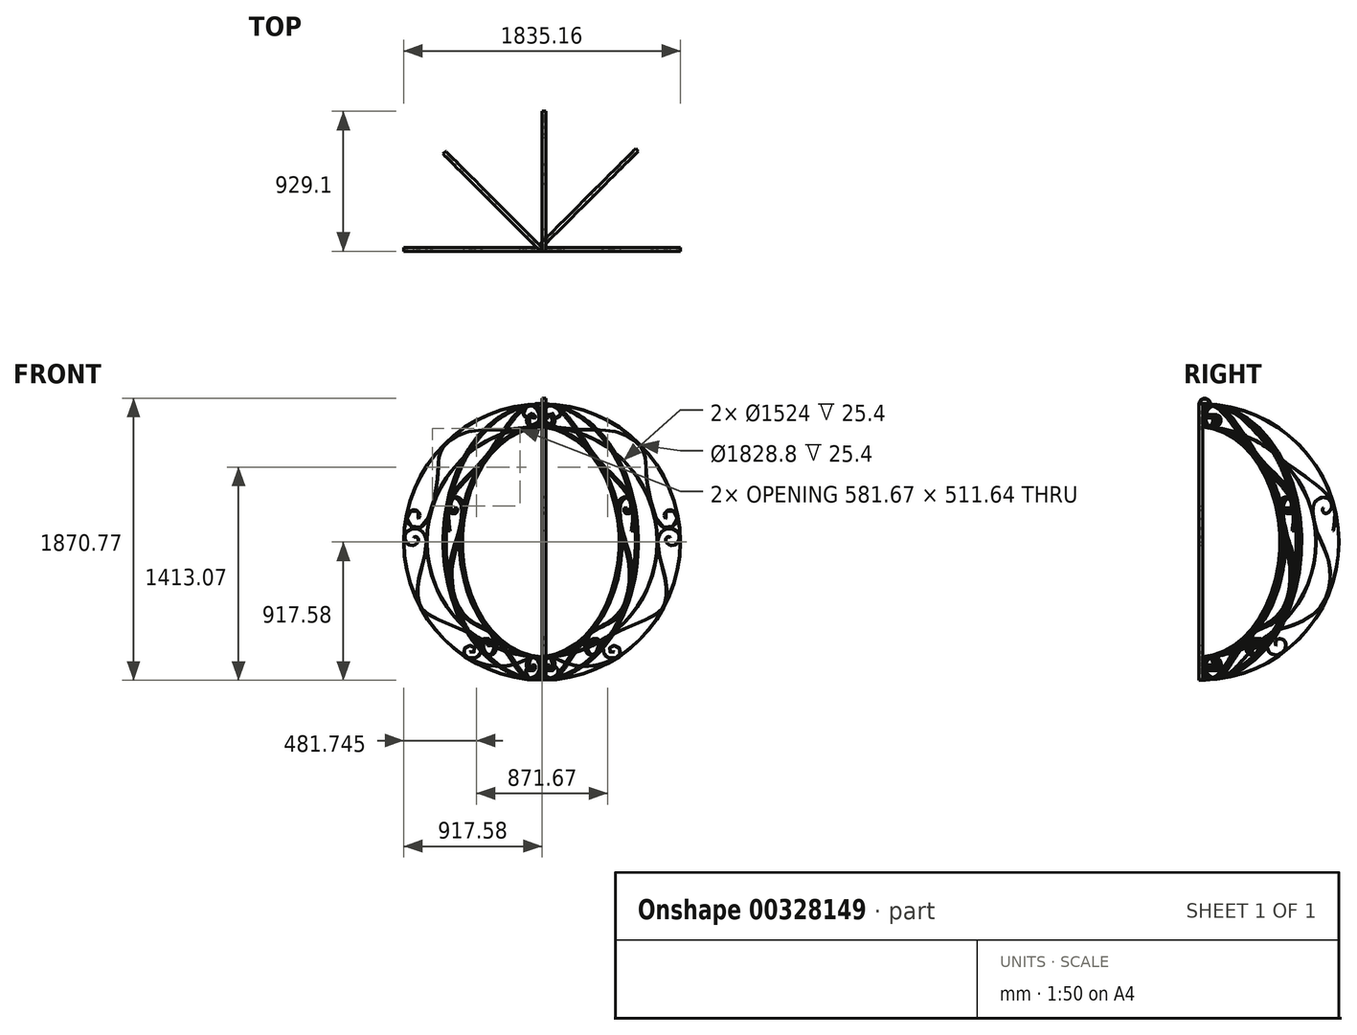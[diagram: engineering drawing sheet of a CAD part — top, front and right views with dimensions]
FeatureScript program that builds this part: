
annotation { "Feature Type Name" : "Feature", "Feature Type Description" : "" }
export const myFeature = defineFeature(function(context is Context, id is Id, definition is map)
    precondition{}
    {
        {
            var Q0;
            Q0=qCreatedBy(makeId("Front.planeOp"),FACE);
            var sketch = newSketch(context, id + "F0", { "sketchPlane" : qUnion([Q0])});
            skCircle(sketch, "E0", {"center": v(0, 0) * mm, "radius": 914.4 * mm});
            skCircle(sketch, "E1.0", {"center": v(0, 0) * mm, "radius": 917.58 * mm});
            skSolve(sketch);
        }
        {
            var Q0;
            Q0 = qSketchRegion(id + "F0", true);
            extrude(context, id + "F1", {"entities" : qUnion([Q0]), "depth" : 25.4 * mm});
        }
        {
            var Q0;
            Q0=qCreatedBy(makeId("Front.planeOp"),FACE);
            var sketch = newSketch(context, id + "F2", { "sketchPlane" : qUnion([Q0])});
            skCircle(sketch, "E2", {"center": v(0, 0) * mm, "radius": 762 * mm});
            skCircle(sketch, "E3.0", {"center": v(0, 0) * mm, "radius": 765.18 * mm});
            skSolve(sketch);
        }
        {
            var Q0;
            Q0 = qSketchRegion(id + "F2", true);
            extrude(context, id + "F3", {"entities" : qUnion([Q0]), "depth" : 25.4 * mm});
        }
        {
            var Q0;
            Q0=qCreatedBy(makeId("Right.planeOp"),FACE);
            var sketch = newSketch(context, id + "F4", { "sketchPlane" : qUnion([Q0])});
            skArc(sketch, "E4", {"start": v(0, -917.18) * mm, "mid": v(903.58, 0.32) * mm, "end": v(0, 917.8) * mm});
            skArc(sketch, "E5.0", {"start": v(-0.05, -914) * mm, "mid": v(900.4, 0.32) * mm, "end": v(-0.05, 914.63) * mm});
            skLineSegment(sketch, "E6", {"start": v(0, 917.8) * mm, "end": v(-0.05, 914.63) * mm});
            skLineSegment(sketch, "E7", {"start": v(0, -917.18) * mm, "end": v(-0.05, -914) * mm});
            skSolve(sketch);
        }
        {
            var Q0;
            Q0 = qSketchRegion(id + "F4", true);
            extrude(context, id + "F5", {"entities" : qUnion([Q0]), "depth" : 25.4 * mm});
        }
        {
            var Q0;
            Q0=qCreatedBy(makeId("Right.planeOp"),FACE);
            var sketch = newSketch(context, id + "F6", { "sketchPlane" : qUnion([Q0])});
            skArc(sketch, "E8.0", {"start": v(-2.38, -761.62) * mm, "mid": v(748, 0.32) * mm, "end": v(-2.38, 762.25) * mm});
            skArc(sketch, "E9.0", {"start": v(-2.33, -764.8) * mm, "mid": v(751.18, 0.32) * mm, "end": v(-2.33, 765.43) * mm});
            skLineSegment(sketch, "E10", {"start": v(-2.33, 765.43) * mm, "end": v(-2.38, 762.25) * mm});
            skLineSegment(sketch, "E11", {"start": v(-2.38, -761.62) * mm, "end": v(-2.33, -764.8) * mm});
            skSolve(sketch);
        }
        {
            var Q0;
            Q0 = qSketchRegion(id + "F6", true);
            extrude(context, id + "F7", {"entities" : qUnion([Q0]), "depth" : 25.4 * mm});
        }
        {
            var Q0;
            Q0=qCreatedBy(makeId("Front.planeOp"),FACE);
            var sketch = newSketch(context, id + "F8", { "sketchPlane" : qUnion([Q0])});
            skFitSpline(sketch, "E12", {"points": [v(-766.38, 0) * mm, v(-837.55, 89.66) * mm, v(-910.52, 47.32) * mm, v(-875.84, -22.95) * mm, v(-820.43, 0) * mm, v(-827.64, 32) * mm, v(-851.96, 32.9) * mm], "startDerivative": vector(22.8, 710.17) * mm, "endDerivative": vector(-220.68, -142.8) * mm});
            skFitSpline(sketch, "E13.0", {"points": [v(-769.55, 0.1) * mm, v(-769.32, 7.3) * mm, v(-770.23, 20.87) * mm, v(-775.14, 38.64) * mm, v(-783.04, 53.79) * mm, v(-793.39, 66.24) * mm, v(-805.67, 75.92) * mm, v(-817.08, 81.59) * mm, v(-826.65, 84.63) * mm, v(-833.97, 86.15) * mm, v(-841.37, 86.89) * mm, v(-848.8, 86.87) * mm, v(-856.18, 86.12) * mm, v(-865.82, 84.18) * mm, v(-877.28, 80.11) * mm, v(-887.37, 74.08) * mm, v(-894.27, 68.25) * mm, v(-898.78, 63.41) * mm, v(-902.56, 58.16) * mm, v(-905.03, 53.46) * mm, v(-906.57, 49.53) * mm, v(-907.5, 46.5) * mm, v(-908.2, 43.37) * mm, v(-908.82, 39.08) * mm, v(-909.04, 33.54) * mm, v(-908.47, 26.73) * mm, v(-907.1, 19.9) * mm, v(-904.28, 10.9) * mm, v(-900.1, 2.4) * mm, v(-894.8, -5.1) * mm, v(-890.37, -10.09) * mm, v(-885.52, -14.33) * mm, v(-881.2, -17.13) * mm, v(-877.64, -18.9) * mm, v(-874.9, -19.96) * mm, v(-872.12, -20.77) * mm, v(-868.3, -21.52) * mm, v(-863.42, -21.86) * mm, v(-857.45, -21.4) * mm, v(-851.53, -20.12) * mm, v(-845.77, -18.13) * mm, v(-840.33, -15.51) * mm, v(-835.32, -12.36) * mm, v(-830.9, -8.79) * mm, v(-827.8, -5.55) * mm, v(-825.74, -2.86) * mm, v(-824.41, -0.82) * mm, v(-823.32, 1.23) * mm, v(-822.18, 3.98) * mm, v(-821.3, 7.47) * mm, v(-821.02, 11.64) * mm, v(-821.46, 15.71) * mm, v(-822.54, 19.6) * mm, v(-824.18, 23.18) * mm, v(-826.3, 26.33) * mm, v(-828.77, 28.95) * mm, v(-831.5, 30.94) * mm, v(-834.46, 32.33) * mm, v(-837.57, 33.13) * mm, v(-840.78, 33.34) * mm, v(-845.1, 32.82) * mm, v(-848.26, 31.52) * mm, v(-850.24, 30.24) * mm]});
            skLineSegment(sketch, "E14", {"start": v(-851.96, 32.9) * mm, "end": v(-850.24, 30.24) * mm});
            skLineSegment(sketch, "E15", {"start": v(-769.54, 0.6) * mm, "end": v(-766.38, 0) * mm});
            skFitSpline(sketch, "E16", {"points": [v(-766.38, 0) * mm, v(-810.04, -219.1) * mm, v(-823.98, -348.98) * mm, v(-806.41, -421.67) * mm, v(-750.28, -479.94) * mm, v(-511.26, -589.61) * mm, v(-410.71, -659.86) * mm, v(-408.3, -740.12) * mm, v(-452.14, -773.78) * mm, v(-507.86, -758.17) * mm, v(-518.27, -709.63) * mm, v(-480.54, -685.55) * mm, v(-448.1, -700.97) * mm, v(-449.4, -729.8) * mm, v(-479.45, -728.28) * mm], "startDerivative": vector(-67.53, -2503.48) * mm, "endDerivative": vector(-624.87, 867.88) * mm});
            skFitSpline(sketch, "E17.0", {"points": [v(-769.55, 0.09) * mm, v(-770.25, -25.85) * mm, v(-773.72, -60.69) * mm, v(-781.3, -101.2) * mm, v(-788, -129.16) * mm, v(-795.25, -155.26) * mm, v(-801.36, -175.92) * mm, v(-806.06, -192.06) * mm, v(-809.43, -204.05) * mm, v(-812.58, -215.99) * mm, v(-815.46, -227.93) * mm, v(-818.03, -239.86) * mm, v(-821.07, -255.7) * mm, v(-824.13, -275.3) * mm, v(-826.58, -298.2) * mm, v(-827.59, -316.6) * mm, v(-827.77, -330.75) * mm, v(-827.59, -341.06) * mm, v(-827.08, -351.04) * mm, v(-826.26, -360.65) * mm, v(-825.1, -369.9) * mm, v(-823.14, -381.8) * mm, v(-820.52, -393.03) * mm, v(-817.25, -403.66) * mm, v(-814.47, -411.34) * mm, v(-811.89, -417.5) * mm, v(-809.65, -422.3) * mm, v(-807.31, -427) * mm, v(-804.16, -432.75) * mm, v(-799.9, -439.46) * mm, v(-795.08, -446) * mm, v(-789.62, -452.44) * mm, v(-783.43, -458.78) * mm, v(-776.42, -465.09) * mm, v(-768.5, -471.4) * mm, v(-761.08, -476.7) * mm, v(-754.6, -480.98) * mm, v(-747.73, -485.3) * mm, v(-738.46, -490.8) * mm, v(-726.32, -497.48) * mm, v(-713.3, -504.26) * mm, v(-699.5, -511.11) * mm, v(-680.2, -520.31) * mm, v(-654.74, -531.88) * mm, v(-622.93, -545.72) * mm, v(-590.8, -559.33) * mm, v(-564.55, -570.34) * mm, v(-544.34, -578.87) * mm, v(-529.7, -585.1) * mm, v(-518, -590.13) * mm, v(-509.04, -594.05) * mm, v(-500.33, -597.9) * mm, v(-489.94, -602.62) * mm, v(-478.28, -608.18) * mm, v(-467.45, -613.72) * mm, v(-454.12, -621.16) * mm, v(-442.48, -628.82) * mm, v(-432.58, -636.96) * mm, v(-426.02, -643.37) * mm, v(-420.33, -650.15) * mm, v(-416.3, -656.18) * mm, v(-413.5, -661.28) * mm, v(-411.63, -665.25) * mm, v(-409.95, -669.35) * mm, v(-408, -674.99) * mm, v(-406.07, -682.28) * mm, v(-404.09, -694.27) * mm, v(-403.75, -706.43) * mm, v(-405, -718.15) * mm, v(-406.72, -726.57) * mm, v(-408.78, -733.13) * mm, v(-410.8, -738.03) * mm, v(-413.05, -742.68) * mm, v(-416.3, -748.02) * mm, v(-420.85, -753.68) * mm, v(-425.99, -758.6) * mm, v(-431.66, -762.74) * mm, v(-437.83, -766.13) * mm, v(-444.43, -768.74) * mm, v(-451.42, -770.56) * mm, v(-458.75, -771.58) * mm, v(-466.29, -771.77) * mm, v(-473.85, -771.13) * mm, v(-481.26, -769.66) * mm, v(-488.36, -767.37) * mm, v(-494.98, -764.25) * mm, v(-499.97, -760.98) * mm, v(-503.58, -757.97) * mm, v(-506.07, -755.52) * mm, v(-508.35, -752.85) * mm, v(-511.1, -749.05) * mm, v(-513.96, -743.9) * mm, v(-516.44, -737.29) * mm, v(-517.9, -730.48) * mm, v(-518.28, -723.71) * mm, v(-517.68, -718.29) * mm, v(-516.63, -714.19) * mm, v(-515.75, -711.75) * mm, v(-514.9, -709.87) * mm, v(-513.95, -708.05) * mm, v(-512.59, -705.85) * mm, v(-510.69, -703.36) * mm, v(-507.84, -700.26) * mm, v(-503.74, -696.8) * mm, v(-498.14, -693.4) * mm, v(-492.1, -690.84) * mm, v(-486.87, -689.47) * mm, v(-482.68, -688.86) * mm, v(-479.57, -688.65) * mm, v(-476.5, -688.69) * mm, v(-472.48, -689.06) * mm, v(-467.65, -690.1) * mm, v(-462.32, -692.2) * mm, v(-457.6, -695.06) * mm, v(-454.3, -698) * mm, v(-452.1, -700.64) * mm, v(-450.68, -702.76) * mm, v(-449.5, -705.01) * mm, v(-448.25, -708.17) * mm, v(-447.32, -712.32) * mm, v(-447.26, -717.32) * mm, v(-448.11, -721.26) * mm, v(-449.33, -724.15) * mm, v(-450.52, -726.16) * mm, v(-451.97, -728) * mm, v(-453.73, -729.66) * mm, v(-455.75, -731.1) * mm, v(-458.69, -732.63) * mm, v(-461.9, -733.5) * mm, v(-465.15, -733.6) * mm, v(-467.58, -733.24) * mm, v(-469.98, -732.42) * mm, v(-472.35, -731.09) * mm, v(-474.66, -729.16) * mm, v(-476.15, -727.42) * mm, v(-476.87, -726.42) * mm]});
            skLineSegment(sketch, "E18", {"start": v(-476.87, -726.42) * mm, "end": v(-479.45, -728.28) * mm});
            skLineSegment(sketch, "E19", {"start": v(-769.54, 0.6) * mm, "end": v(-769.55, 0.09) * mm});
            skSolve(sketch);
        }
        {
            var Q0;
            Q0 = qSketchRegion(id + "F8", true);
            extrude(context, id + "F9", {"entities" : qUnion([Q0]), "depth" : 25.4 * mm});
        }
        {
            var Q0;
            Q0=qCreatedBy(makeId("Front.planeOp"),FACE);
            var sketch = newSketch(context, id + "F10", { "sketchPlane" : qUnion([Q0])});
            skFitSpline(sketch, "E20", {"points": [v(-820.36, 153.24) * mm, v(-841.55, 212.18) * mm, v(-892.93, 185.39) * mm, v(-881.98, 116.68) * mm, v(-813.57, 92.5) * mm, v(-752.31, 165.46) * mm, v(-689.96, 435.02) * mm, v(-666.43, 608.75) * mm, v(-499.45, 727.2) * mm, v(-204.24, 745.98) * mm, v(0, 812.46) * mm, v(-26.01, 898.7) * mm, v(-99.89, 903.2) * mm, v(-127.82, 855) * mm, v(-91.33, 819.42) * mm, v(-62.97, 856.62) * mm], "startDerivative": vector(1522.53, 1759.37) * mm, "endDerivative": vector(-990.2, 1432.62) * mm});
            skFitSpline(sketch, "E21.0", {"points": [v(-822.76, 155.31) * mm, v(-820.87, 157.5) * mm, v(-817.7, 161.76) * mm, v(-814.56, 167.83) * mm, v(-812.87, 173.51) * mm, v(-812.4, 178.82) * mm, v(-813.03, 183.8) * mm, v(-814.61, 188.46) * mm, v(-817.06, 192.8) * mm, v(-820.26, 196.8) * mm, v(-824.1, 200.36) * mm, v(-828.45, 203.46) * mm, v(-833.16, 206.02) * mm, v(-837.25, 207.67) * mm, v(-840.55, 208.68) * mm, v(-843.84, 209.47) * mm, v(-847.9, 210.06) * mm, v(-852.7, 210.16) * mm, v(-858.95, 209.53) * mm, v(-866.42, 207.4) * mm, v(-874.6, 202.92) * mm, v(-880.57, 197.8) * mm, v(-884.67, 193.02) * mm, v(-887.39, 189.13) * mm, v(-889.7, 184.96) * mm, v(-891.6, 180.54) * mm, v(-893.07, 175.9) * mm, v(-894.46, 169.47) * mm, v(-895.16, 161.07) * mm, v(-894.32, 150.73) * mm, v(-891.86, 140.49) * mm, v(-888.49, 132.31) * mm, v(-885.03, 126.15) * mm, v(-882.06, 121.76) * mm, v(-878.72, 117.64) * mm, v(-875.01, 113.81) * mm, v(-870.98, 110.28) * mm, v(-865.21, 105.98) * mm, v(-857.38, 101.43) * mm, v(-847.34, 97.38) * mm, v(-837, 94.86) * mm, v(-828.42, 94.11) * mm, v(-821.77, 94.36) * mm, v(-816.92, 94.98) * mm, v(-812.27, 96.04) * mm, v(-806.31, 98.03) * mm, v(-799.26, 101.63) * mm, v(-791.3, 107.7) * mm, v(-781.24, 118.13) * mm, v(-771.9, 132) * mm, v(-763.03, 149.04) * mm, v(-756.54, 163.35) * mm, v(-750.13, 179.1) * mm, v(-741.72, 201.83) * mm, v(-731.61, 233.05) * mm, v(-720.45, 273.67) * mm, v(-712.24, 309.06) * mm, v(-706.5, 337.65) * mm, v(-702.64, 359.06) * mm, v(-699.28, 380.28) * mm, v(-696.93, 397.66) * mm, v(-695.34, 411.31) * mm, v(-694.3, 421.4) * mm, v(-693.41, 431.31) * mm, v(-692.7, 441.03) * mm, v(-692.11, 450.56) * mm, v(-691.5, 463.03) * mm, v(-690.97, 478.18) * mm, v(-690.48, 495.7) * mm, v(-689.73, 518.26) * mm, v(-688.4, 539.71) * mm, v(-685.6, 560.23) * mm, v(-682.54, 575.2) * mm, v(-679, 587.35) * mm, v(-675.44, 596.89) * mm, v(-672.4, 603.95) * mm, v(-668.95, 610.94) * mm, v(-665.07, 617.84) * mm, v(-660.77, 624.63) * mm, v(-654.52, 633.54) * mm, v(-645.76, 644.4) * mm, v(-633.83, 656.88) * mm, v(-620.62, 668.78) * mm, v(-601.44, 683.77) * mm, v(-574.8, 700.72) * mm, v(-545.38, 714.84) * mm, v(-520.62, 724.17) * mm, v(-501.54, 730.12) * mm, v(-482.09, 734.95) * mm, v(-455.7, 740.02) * mm, v(-421.92, 744.13) * mm, v(-380.25, 746.46) * mm, v(-337.58, 747.14) * mm, v(-294.04, 747.12) * mm, v(-257.16, 747.31) * mm, v(-227.36, 748.06) * mm, v(-204.88, 749.04) * mm, v(-182.28, 750.55) * mm, v(-152.34, 753.34) * mm, v(-115.93, 758.4) * mm, v(-82.65, 765.86) * mm, v(-58.99, 773.43) * mm, v(-43, 779.95) * mm, v(-29.04, 787.33) * mm, v(-19.33, 794.2) * mm, v(-12.84, 800.12) * mm, v(-8.63, 804.78) * mm, v(-5.7, 808.84) * mm, v(-3.7, 812.2) * mm, v(-1.93, 815.62) * mm, v(-0.17, 820.07) * mm, v(1.78, 827.49) * mm, v(2.64, 837.21) * mm, v(1.35, 849.22) * mm, v(-2.05, 861.13) * mm, v(-7.3, 872.5) * mm, v(-12.98, 881.15) * mm, v(-18.19, 887.37) * mm, v(-22.38, 891.63) * mm, v(-26.82, 895.43) * mm, v(-31.47, 898.72) * mm, v(-36.32, 901.52) * mm, v(-43.01, 904.62) * mm, v(-51.71, 907.32) * mm, v(-62.41, 908.78) * mm, v(-73.08, 908.53) * mm, v(-83.42, 906.69) * mm, v(-91.51, 903.9) * mm, v(-97.52, 900.97) * mm, v(-103.18, 897.59) * mm, v(-109.55, 892.58) * mm, v(-115.87, 885.56) * mm, v(-120.7, 877.79) * mm, v(-123.85, 869.51) * mm, v(-124.97, 862.4) * mm, v(-124.89, 857.4) * mm, v(-124.58, 854.56) * mm, v(-124.1, 851.7) * mm, v(-123.2, 848.16) * mm, v(-121.1, 842.64) * mm, v(-117.35, 836.17) * mm, v(-112.3, 830.75) * mm, v(-107.62, 827.3) * mm, v(-103.82, 825.22) * mm, v(-99.76, 823.68) * mm, v(-96.17, 822.9) * mm, v(-93.18, 822.62) * mm, v(-90.12, 822.56) * mm, v(-86.11, 822.93) * mm, v(-81.24, 824.07) * mm, v(-76.5, 825.85) * mm, v(-72.12, 828.2) * mm, v(-68.3, 831.03) * mm, v(-65.2, 834.26) * mm, v(-63.01, 837.79) * mm, v(-61.8, 841.52) * mm, v(-61.64, 845.51) * mm, v(-62.7, 849.9) * mm, v(-64.41, 853.13) * mm, v(-65.58, 854.81) * mm]});
            skLineSegment(sketch, "E22", {"start": v(-822.76, 155.31) * mm, "end": v(-820.36, 153.24) * mm});
            skLineSegment(sketch, "E23", {"start": v(-62.97, 856.62) * mm, "end": v(-65.58, 854.81) * mm});
            skSolve(sketch);
        }
        {
            var Q0;
            Q0 = qSketchRegion(id + "F10", true);
            extrude(context, id + "F11", {"entities" : qUnion([Q0]), "operationType" : NewBodyOperationType.ADD, "depth" : 25.4 * mm});
        }
        {
            var Q0;
            Q0=makeQuery(id+"F3.opExtrude","SWEPT_BODY",BODY,{"disambiguationData":[OSD([sQuery(id+"F2.wireOp",EDGE,"E2"),sQuery(id+"F2.wireOp",EDGE,"E3.0")])]});
            var Q1;
            Q1=makeQuery(id+"F9.opExtrude","SWEPT_BODY",BODY,{"disambiguationData":[OSD([sQuery(id+"F8.wireOp",EDGE,"E12"),sQuery(id+"F8.wireOp",EDGE,"E13.0"),sQuery(id+"F8.wireOp",EDGE,"E14"),sQuery(id+"F8.wireOp",EDGE,"E16"),sQuery(id+"F8.wireOp",EDGE,"E17.0"),sQuery(id+"F8.wireOp",EDGE,"E18"),sQuery(id+"F8.wireOp",EDGE,"E19")])]});
            var Q2;
            Q2=qCreatedBy(makeId("Right.planeOp"),FACE);
            mirror(context, id + "F12", {"entities" : qUnion([Q0, Q1]), "mirrorPlane" : qUnion([Q2])});
        }
        {
            var Q0;
            Q0=qCreatedBy(makeId("Front.planeOp"),FACE);
            var sketch = newSketch(context, id + "F13", { "sketchPlane" : qUnion([Q0])});
            skFitSpline(sketch, "E24", {"points": [v(-464.75, -784.96) * mm, v(-336.85, -822.2) * mm, v(-177.25, -811.88) * mm, v(-50.25, -767.12) * mm, v(6.22, -822.74) * mm, v(-19.78, -898.37) * mm, v(-84.79, -899.63) * mm, v(-106.14, -857) * mm, v(-87.31, -826.93) * mm, v(-50.93, -839.36) * mm], "startDerivative": vector(1405.33, -534.22) * mm, "endDerivative": vector(261.46, -709.68) * mm});
            skFitSpline(sketch, "E25.0", {"points": [v(-463.62, -781.99) * mm, v(-448.99, -787.55) * mm, v(-430.27, -794.58) * mm, v(-409.86, -801.8) * mm, v(-396.34, -806.28) * mm, v(-384.13, -809.93) * mm, v(-372.74, -812.88) * mm, v(-361.68, -815.27) * mm, v(-352.3, -816.9) * mm, v(-344.47, -818.04) * mm, v(-338.36, -818.83) * mm, v(-331.95, -819.58) * mm, v(-323.03, -820.5) * mm, v(-311.2, -821.5) * mm, v(-296.15, -822.34) * mm, v(-280.38, -822.72) * mm, v(-264.08, -822.53) * mm, v(-247.43, -821.7) * mm, v(-230.6, -820.11) * mm, v(-213.78, -817.68) * mm, v(-199.9, -814.87) * mm, v(-188.97, -812.1) * mm, v(-180.89, -809.75) * mm, v(-172.93, -807.12) * mm, v(-165.1, -804.22) * mm, v(-157.37, -801.12) * mm, v(-147.22, -796.75) * mm, v(-134.82, -791.03) * mm, v(-120.4, -784.1) * mm, v(-106.4, -777.55) * mm, v(-92.85, -771.76) * mm, v(-79.67, -767.15) * mm, v(-68.98, -764.65) * mm, v(-60.58, -763.7) * mm, v(-55.4, -763.58) * mm, v(-51.29, -763.8) * mm, v(-47.2, -764.26) * mm, v(-42.2, -765.25) * mm, v(-36.37, -767.07) * mm, v(-28.88, -770.28) * mm, v(-20.12, -775.65) * mm, v(-10.75, -783.92) * mm, v(-2.76, -793.73) * mm, v(2.6, -802.93) * mm, v(6, -810.76) * mm, v(8.06, -816.83) * mm, v(9.63, -823.07) * mm, v(10.66, -829.41) * mm, v(11.18, -835.81) * mm, v(11.2, -844.37) * mm, v(10.02, -854.98) * mm, v(6.77, -867.24) * mm, v(1.8, -878.68) * mm, v(-3.73, -887.23) * mm, v(-8.93, -893.3) * mm, v(-13.21, -897.41) * mm, v(-17.1, -900.44) * mm, v(-20.38, -902.58) * mm, v(-23.76, -904.54) * mm, v(-28.15, -906.65) * mm, v(-35.44, -909.3) * mm, v(-44.93, -911.31) * mm, v(-56.47, -911.75) * mm, v(-65.85, -910.54) * mm, v(-73.01, -908.66) * mm, v(-78.15, -906.8) * mm, v(-82.2, -904.87) * mm, v(-85.26, -903.11) * mm, v(-88.2, -901.2) * mm, v(-91.62, -898.56) * mm, v(-96.51, -893.86) * mm, v(-101.57, -887.23) * mm, v(-105.94, -878.48) * mm, v(-108.63, -869.3) * mm, v(-109.48, -861.62) * mm, v(-109.31, -855.62) * mm, v(-108.57, -849.78) * mm, v(-106.6, -842.85) * mm, v(-102.55, -835.4) * mm, v(-97.81, -830.11) * mm, v(-93.25, -826.6) * mm, v(-89.46, -824.35) * mm, v(-85.3, -822.51) * mm, v(-80.87, -821.16) * mm, v(-76.24, -820.35) * mm, v(-71.5, -820.2) * mm, v(-66.76, -820.79) * mm, v(-62.12, -822.24) * mm, v(-57.74, -824.64) * mm, v(-53.8, -828.08) * mm, v(-50.45, -832.55) * mm, v(-48.7, -836.24) * mm, v(-47.95, -838.26) * mm]});
            skLineSegment(sketch, "E26", {"start": v(-463.62, -781.99) * mm, "end": v(-464.75, -784.96) * mm});
            skLineSegment(sketch, "E27", {"start": v(-47.95, -838.26) * mm, "end": v(-50.93, -839.36) * mm});
            skSolve(sketch);
        }
        {
            var Q0;
            Q0 = qSketchRegion(id + "F13", true);
            extrude(context, id + "F14", {"entities" : qUnion([Q0]), "depth" : 25.4 * mm});
        }
        {
            var Q0;
            Q0=makeQuery(id+"F14.opExtrude","SWEPT_BODY",BODY,{"disambiguationData":[OSD([sQuery(id+"F13.wireOp",EDGE,"E24"),sQuery(id+"F13.wireOp",EDGE,"E25.0"),sQuery(id+"F13.wireOp",EDGE,"E26"),sQuery(id+"F13.wireOp",EDGE,"E27")])]});
            var Q1;
            Q1=qCreatedBy(makeId("Right.planeOp"),FACE);
            mirror(context, id + "F15", {"operationType" : NewBodyOperationType.ADD, "entities" : qUnion([Q0]), "mirrorPlane" : qUnion([Q1])});
        }
        {
            var Q0;
            Q0=qCreatedBy(makeId("Right.planeOp"),FACE);
            var sketch = newSketch(context, id + "F16", { "sketchPlane" : qUnion([Q0])});
            skFitSpline(sketch, "E28", {"points": [v(58.89, 821.78) * mm, v(105.76, 839.02) * mm, v(112.38, 781.02) * mm, v(35.54, 767.65) * mm, v(0, 825.81) * mm, v(31.08, 887.16) * mm, v(132.75, 900.64) * mm, v(346.4, 734.22) * mm, v(538.07, 539.86) * mm, v(836.34, 299.56) * mm, v(877.14, 163) * mm, v(865, 72.14) * mm], "startDerivative": vector(89.14, 1381.73) * mm, "endDerivative": vector(-221.8, -1107.85) * mm});
            skFitSpline(sketch, "E29.0", {"points": [v(62.06, 821.58) * mm, v(62.16, 823.22) * mm, v(62.6, 826.25) * mm, v(63.87, 830.12) * mm, v(65.63, 833.36) * mm, v(67.83, 836.05) * mm, v(70.43, 838.25) * mm, v(74.39, 840.54) * mm, v(80.13, 842.26) * mm, v(87.74, 842.48) * mm, v(94.12, 841.2) * mm, v(98.9, 839.36) * mm, v(101.7, 837.9) * mm, v(103.77, 836.56) * mm, v(105.73, 835.1) * mm, v(108.88, 832.27) * mm, v(112.58, 827.43) * mm, v(115.73, 820.64) * mm, v(117.53, 813.2) * mm, v(117.94, 805.42) * mm, v(116.95, 797.69) * mm, v(114.96, 791.56) * mm, v(112.67, 787.02) * mm, v(110.61, 783.83) * mm, v(108.2, 780.9) * mm, v(105.44, 778.18) * mm, v(102.35, 775.7) * mm, v(97.83, 772.73) * mm, v(91.5, 769.62) * mm, v(83.1, 766.92) * mm, v(71.17, 764.73) * mm, v(58.72, 764.7) * mm, v(46.89, 766.85) * mm, v(39.98, 769.1) * mm, v(34.9, 771.42) * mm, v(30.09, 774.1) * mm, v(24.6, 778.05) * mm, v(18.87, 783.66) * mm, v(12.36, 792.12) * mm, v(7.6, 801.78) * mm, v(4.65, 812.07) * mm, v(3.58, 818.64) * mm, v(3.2, 823.91) * mm, v(3.12, 829.16) * mm, v(3.61, 835.67) * mm, v(5.1, 843.34) * mm, v(8.25, 853.3) * mm, v(14.26, 865.14) * mm, v(24.51, 877.85) * mm, v(37.53, 888.6) * mm, v(53.02, 896.9) * mm, v(70.75, 902.37) * mm, v(87.18, 904.19) * mm, v(101.2, 903.78) * mm, v(112.12, 902.5) * mm, v(123.4, 900.16) * mm, v(135.04, 896.72) * mm, v(147, 892.15) * mm, v(163.33, 884.64) * mm, v(184.35, 872.8) * mm, v(210.18, 855.28) * mm, v(236.26, 835.09) * mm, v(262.28, 812.84) * mm, v(283.62, 793.12) * mm, v(300.34, 776.94) * mm, v(312.66, 764.7) * mm, v(324.71, 752.4) * mm, v(334.51, 742.2) * mm, v(342.18, 734.08) * mm, v(349.72, 726.03) * mm, v(358.94, 716.06) * mm, v(369.72, 704.24) * mm, v(383.8, 688.66) * mm, v(401, 669.46) * mm, v(421.54, 646.76) * mm, v(442.47, 624.25) * mm, v(464.29, 601.83) * mm, v(483.63, 583.1) * mm, v(500.06, 568.05) * mm, v(512.9, 556.7) * mm, v(524.12, 547.19) * mm, v(533.42, 539.53) * mm, v(542.95, 531.84) * mm, v(555.28, 522.18) * mm, v(570.64, 510.51) * mm, v(586.48, 498.77) * mm, v(608.1, 483.03) * mm, v(635.83, 463.2) * mm, v(669.48, 439.25) * mm, v(702.72, 415.18) * mm, v(734.8, 391.08) * mm, v(764.94, 367) * mm, v(787.8, 347.03) * mm, v(804.34, 331.14) * mm, v(815.79, 319.29) * mm, v(824.43, 309.47) * mm, v(830.77, 301.65) * mm, v(836.7, 293.87) * mm, v(843.36, 284.2) * mm, v(850.22, 272.67) * mm, v(856.04, 261.24) * mm, v(862.5, 246.15) * mm, v(868.35, 227.58) * mm, v(872.43, 205.84) * mm, v(873.88, 188.25) * mm, v(874.19, 174.54) * mm, v(874.05, 164.45) * mm, v(873.65, 154.56) * mm, v(872.77, 141.66) * mm, v(871.13, 126) * mm, v(868.47, 107.83) * mm, v(865.32, 90.11) * mm, v(863.04, 78.53) * mm, v(861.88, 72.76) * mm]});
            skLineSegment(sketch, "E30", {"start": v(58.89, 821.78) * mm, "end": v(62.06, 821.58) * mm});
            skLineSegment(sketch, "E31", {"start": v(861.88, 72.76) * mm, "end": v(865, 72.14) * mm});
            skSolve(sketch);
        }
        {
            var Q0;
            Q0 = qSketchRegion(id + "F16", true);
            extrude(context, id + "F17", {"entities" : qUnion([Q0]), "depth" : 25.4 * mm});
        }
        {
            var Q0;
            Q0=qCreatedBy(makeId("Right.planeOp"),FACE);
            var sketch = newSketch(context, id + "F18", { "sketchPlane" : qUnion([Q0])});
            skFitSpline(sketch, "E32", {"points": [v(833, 192.73) * mm, v(858.99, 238.6) * mm, v(822.76, 294.38) * mm, v(739, 262.86) * mm, v(766.82, 40.25) * mm, v(837.49, -148.84) * mm, v(787.26, -420.34) * mm, v(575.48, -557.66) * mm, v(454.42, -604.84) * mm, v(420.89, -673.4) * mm, v(454.8, -743.96) * mm, v(533.65, -730.04) * mm, v(544.13, -657.03) * mm, v(490.71, -646.47) * mm, v(485.85, -687.83) * mm], "startDerivative": vector(737.01, 571.07) * mm, "endDerivative": vector(709.47, -766.23) * mm});
            skFitSpline(sketch, "E33", {"points": [v(833, 192.73) * mm, v(801.88, 192.73) * mm, v(796.21, 227.08) * mm], "startDerivative": vector(-54.77, -28.8) * mm, "endDerivative": vector(41.92, 61.2) * mm});
            skFitSpline(sketch, "E34.0", {"points": [v(831.05, 195.24) * mm, v(834.7, 198.07) * mm, v(840.33, 203.44) * mm, v(846.9, 212.3) * mm, v(851.04, 219.65) * mm, v(853.6, 226.24) * mm, v(854.99, 231.73) * mm, v(855.66, 235.94) * mm, v(855.93, 240.23) * mm, v(855.79, 244.62) * mm, v(855.23, 249.06) * mm, v(853.96, 255) * mm, v(851.4, 262.35) * mm, v(846.88, 270.72) * mm, v(841, 278.33) * mm, v(835.08, 283.77) * mm, v(829.77, 287.42) * mm, v(825.52, 289.79) * mm, v(821.02, 291.73) * mm, v(816.25, 293.24) * mm, v(811.25, 294.3) * mm, v(804.33, 295.14) * mm, v(795.34, 295.08) * mm, v(784.36, 293.23) * mm, v(773.57, 289.61) * mm, v(763.35, 284.25) * mm, v(755.6, 278.36) * mm, v(750.02, 272.8) * mm, v(746.2, 268.2) * mm, v(742.76, 263.2) * mm, v(739.78, 257.76) * mm, v(737.23, 251.88) * mm, v(734.38, 243.49) * mm, v(731.84, 232) * mm, v(730.32, 216.84) * mm, v(730.2, 195.09) * mm, v(733.27, 165.54) * mm, v(739.8, 134.28) * mm, v(746.55, 109.07) * mm, v(752.23, 90.27) * mm, v(758.4, 71.79) * mm, v(763.82, 56.82) * mm, v(768.27, 45.2) * mm, v(771.64, 36.7) * mm, v(775.03, 28.4) * mm, v(779.57, 17.6) * mm, v(785.27, 4.5) * mm, v(792.07, -10.66) * mm, v(798.76, -25.44) * mm, v(807.46, -44.8) * mm, v(815.69, -63.95) * mm, v(823.17, -83.45) * mm, v(828.33, -98.38) * mm, v(832.97, -113.76) * mm, v(837.03, -129.73) * mm, v(840.43, -146.42) * mm, v(843.1, -163.97) * mm, v(845.01, -182.27) * mm, v(846.13, -201.18) * mm, v(846.4, -220.58) * mm, v(845.64, -246.92) * mm, v(842.45, -280.41) * mm, v(834.77, -320.49) * mm, v(824.94, -352.91) * mm, v(814.88, -377.75) * mm, v(806.2, -395.7) * mm, v(797.97, -409.98) * mm, v(790.8, -420.93) * mm, v(785.1, -428.88) * mm, v(779.12, -436.58) * mm, v(770.79, -446.5) * mm, v(759.73, -458.27) * mm, v(745.57, -471.43) * mm, v(725.66, -487.75) * mm, v(699.2, -505.92) * mm, v(665.92, -524.5) * mm, v(637.77, -537.55) * mm, v(615.5, -546.68) * mm, v(599.06, -552.9) * mm, v(585.67, -557.61) * mm, v(575.21, -561.1) * mm, v(564.94, -564.43) * mm, v(552.48, -568.3) * mm, v(538.16, -572.62) * mm, v(524.52, -576.76) * mm, v(511.59, -580.84) * mm, v(499.42, -585.01) * mm, v(488.04, -589.39) * mm, v(477.51, -594.1) * mm, v(467.85, -599.27) * mm, v(460.56, -604.06) * mm, v(455.18, -608.24) * mm, v(450.11, -612.69) * mm, v(444.35, -618.7) * mm, v(438.37, -626.59) * mm, v(433.37, -635.08) * mm, v(429.39, -644.11) * mm, v(426.45, -653.62) * mm, v(424.6, -663.54) * mm, v(423.86, -673.8) * mm, v(424.3, -684.36) * mm, v(425.88, -694.91) * mm, v(428.62, -705.2) * mm, v(432.5, -714.9) * mm, v(437.5, -723.79) * mm, v(442.58, -730.27) * mm, v(447.17, -734.78) * mm, v(450.88, -737.8) * mm, v(454.2, -740) * mm, v(456.97, -741.54) * mm, v(459.85, -742.94) * mm, v(463.62, -744.44) * mm, v(469.96, -746.3) * mm, v(478.36, -747.58) * mm, v(488.87, -747.49) * mm, v(499.44, -745.79) * mm, v(509.72, -742.52) * mm, v(517.75, -738.52) * mm, v(523.68, -734.6) * mm, v(527.84, -731.3) * mm, v(531.67, -727.64) * mm, v(535.15, -723.62) * mm, v(538.28, -719.3) * mm, v(541.95, -713.17) * mm, v(545.59, -704.98) * mm, v(548.32, -694.73) * mm, v(549.34, -684.5) * mm, v(548.7, -676.37) * mm, v(547.3, -670.32) * mm, v(545.8, -666.06) * mm, v(544.16, -662.77) * mm, v(542.62, -660.33) * mm, v(541.36, -658.6) * mm, v(539.97, -656.95) * mm, v(537.97, -654.87) * mm, v(535.2, -652.5) * mm, v(531.5, -650.02) * mm, v(526.19, -647.26) * mm, v(519.01, -644.87) * mm, v(510.2, -643.79) * mm, v(503.24, -644.45) * mm, v(498.23, -645.92) * mm, v(495.4, -647.22) * mm, v(493.33, -648.48) * mm, v(491.41, -649.9) * mm, v(489.24, -651.97) * mm, v(487.03, -654.88) * mm, v(484.64, -659.22) * mm, v(482.75, -665.31) * mm, v(482.43, -672.91) * mm, v(483.85, -678.83) * mm, v(485.99, -682.98) * mm, v(487.4, -684.82) * mm, v(488.18, -685.67) * mm]});
            skFitSpline(sketch, "E35.0", {"points": [v(831.51, 195.54) * mm, v(829.45, 194.46) * mm, v(825.87, 193.04) * mm, v(820.7, 191.92) * mm, v(816.76, 191.54) * mm, v(812.92, 191.69) * mm, v(809.9, 192.27) * mm, v(807.65, 193.04) * mm, v(806.06, 193.77) * mm, v(804.57, 194.66) * mm, v(803.19, 195.7) * mm, v(801.88, 196.96) * mm, v(800.25, 198.87) * mm, v(798.48, 201.67) * mm, v(796.86, 205.5) * mm, v(795.85, 209.64) * mm, v(795.49, 213.88) * mm, v(795.83, 218.03) * mm, v(796.9, 221.91) * mm, v(798.1, 224.22) * mm, v(798.83, 225.28) * mm]});
            skLineSegment(sketch, "E36", {"start": v(796.21, 227.08) * mm, "end": v(798.83, 225.28) * mm});
            skLineSegment(sketch, "E37", {"start": v(485.85, -687.83) * mm, "end": v(488.18, -685.67) * mm});
            skSolve(sketch);
        }
        {
            var Q0;
            Q0 = qSketchRegion(id + "F18", true);
            extrude(context, id + "F19", {"entities" : qUnion([Q0]), "depth" : 25.4 * mm});
        }
        {
            var Q0;
            Q0=qCreatedBy(makeId("Right.planeOp"),FACE);
            var sketch = newSketch(context, id + "F20", { "sketchPlane" : qUnion([Q0])});
            skFitSpline(sketch, "E38", {"points": [v(422.6, -631.86) * mm, v(290.66, -756.8) * mm, v(134.08, -897.5) * mm, v(24.4, -881.6) * mm, v(0, -815.04) * mm, v(52.25, -763.08) * mm, v(113.65, -784.78) * mm, v(110.63, -846.8) * mm, v(68.27, -848.32) * mm, v(68.27, -814.28) * mm], "startDerivative": vector(-622.17, -631.45) * mm, "endDerivative": vector(390.78, 455.9) * mm});
            skFitSpline(sketch, "E39.0", {"points": [v(420.34, -629.63) * mm, v(413.9, -636.16) * mm, v(399.72, -649.77) * mm, v(375.36, -671.9) * mm, v(353.21, -691.88) * mm, v(334.82, -708.86) * mm, v(320.8, -722.1) * mm, v(309, -733.59) * mm, v(299.57, -743.04) * mm, v(292.5, -750.28) * mm, v(285.44, -757.65) * mm, v(276.1, -767.65) * mm, v(264.48, -780.38) * mm, v(250.62, -795.76) * mm, v(236.81, -811) * mm, v(223, -825.85) * mm, v(209.16, -840.06) * mm, v(195.26, -853.38) * mm, v(181.26, -865.55) * mm, v(167.14, -876.32) * mm, v(155.25, -883.93) * mm, v(145.65, -889.08) * mm, v(138.4, -892.44) * mm, v(131.1, -895.28) * mm, v(123.75, -897.57) * mm, v(116.35, -899.35) * mm, v(106.47, -901.05) * mm, v(94.18, -901.95) * mm, v(79.75, -901.2) * mm, v(65.89, -898.75) * mm, v(52.83, -894.72) * mm, v(40.83, -889.25) * mm, v(31.9, -883.6) * mm, v(25.54, -878.51) * mm, v(19.71, -873.06) * mm, v(13.45, -865.61) * mm, v(7.65, -855.92) * mm, v(3.65, -845.7) * mm, v(1.53, -835.17) * mm, v(1.37, -826.33) * mm, v(2.25, -819.32) * mm, v(3.43, -814.12) * mm, v(5.13, -808.98) * mm, v(8.05, -802.26) * mm, v(12.84, -794.2) * mm, v(20.16, -785.38) * mm, v(28.78, -777.72) * mm, v(36.8, -772.54) * mm, v(43.58, -769.27) * mm, v(48.8, -767.29) * mm, v(54.14, -765.8) * mm, v(59.56, -764.83) * mm, v(65.03, -764.38) * mm, v(72.31, -764.44) * mm, v(81.26, -765.75) * mm, v(91.33, -769.23) * mm, v(98.83, -773.65) * mm, v(104.1, -778.05) * mm, v(107.65, -781.78) * mm, v(110.22, -785.23) * mm, v(112.04, -788.2) * mm, v(113.7, -791.32) * mm, v(115.46, -795.44) * mm, v(117.63, -802.43) * mm, v(119.07, -811.62) * mm, v(118.73, -822.6) * mm, v(116.76, -831.01) * mm, v(114.2, -836.91) * mm, v(112.21, -840.18) * mm, v(110.4, -842.5) * mm, v(108.93, -844.08) * mm, v(107.35, -845.5) * mm, v(105.08, -847.22) * mm, v(101.97, -849) * mm, v(97.9, -850.58) * mm, v(93.6, -851.58) * mm, v(89.23, -852) * mm, v(84.89, -851.88) * mm, v(80.72, -851.2) * mm, v(76.86, -850.01) * mm, v(74, -848.63) * mm, v(71.98, -847.3) * mm, v(70.62, -846.21) * mm, v(69.41, -845.02) * mm, v(67.98, -843.29) * mm, v(66.53, -840.88) * mm, v(65.34, -837.65) * mm, v(64.7, -834.17) * mm, v(64.65, -829.32) * mm, v(66.08, -823.1) * mm, v(68.87, -818.46) * mm, v(70.68, -816.35) * mm]});
            skLineSegment(sketch, "E40", {"start": v(419.84, -630.14) * mm, "end": v(422.6, -631.86) * mm});
            skLineSegment(sketch, "E41", {"start": v(70.68, -816.35) * mm, "end": v(68.27, -814.28) * mm});
            skSolve(sketch);
        }
        {
            var Q0;
            Q0 = qSketchRegion(id + "F20", true);
            extrude(context, id + "F21", {"entities" : qUnion([Q0]), "depth" : 25.4 * mm});
        }
        {
            var Q0;
            Q0=qCreatedBy(makeId("Right.planeOp"),FACE);
            var sketch = newSketch(context, id + "F22", { "sketchPlane" : qUnion([Q0])});
            skArc(sketch, "E42", {"start": v(50.36, 914.83) * mm, "mid": v(13.76, 953.17) * mm, "end": v(-25.52, 917.59) * mm});
            skArc(sketch, "E43.0", {"start": v(44.02, 914.9) * mm, "mid": v(13.53, 946.82) * mm, "end": v(-19.18, 917.2) * mm});
            skLineSegment(sketch, "E44", {"start": v(-25.52, 917.59) * mm, "end": v(-19.18, 917.2) * mm});
            skLineSegment(sketch, "E45", {"start": v(44.02, 914.9) * mm, "end": v(50.36, 914.83) * mm});
            skSolve(sketch);
        }
        {
            var Q0;
            Q0 = qSketchRegion(id + "F22", true);
            extrude(context, id + "F23", {"entities" : qUnion([Q0]), "depth" : 25.4 * mm});
        }
        {
            var Q0;
            Q0=makeQuery(id+"F23.opExtrude","CAP_EDGE",EDGE,{"disambiguationData":[OSD([sQuery(id+"F22.wireOp",EDGE,"E43.0")])],"isStart":false});
            fillet(context, id + "F24", {"entities" : qUnion([Q0]), "radius" : 5.08 * mm, "tangentPropagation" : true, "allowEdgeOverflow" : false});
        }
        {
            var Q0;
            Q0=qCreatedBy(makeId("Top.planeOp"),FACE);
            var sketch = newSketch(context, id + "F25", { "sketchPlane" : qUnion([Q0])});
            skLineSegment(sketch, "E46", {"start": v(0, 0) * mm, "end": v(-7.4, -3.06) * mm, "construction": true});
            skLineSegment(sketch, "E47", {"start": v(0, 0) * mm, "end": v(-8.66, 20.92) * mm, "construction": true});
            skSolve(sketch);
        }
        {
            var Q0;
            Q0=sQuery(id+"F25.wireOp",EDGE,"E47");
            cPlane(context, id + "F26", {"entities" : qUnion([Q0]), "cplaneType" : CPlaneType.LINE_ANGLE, "offset" : 25.4 * mm, "angle" : 90 * degree, "width" : 152.4 * mm, "height" : 152.4 * mm});
        }
        {
            var Q0;
            Q0=makeQuery(id+"F7.opExtrude","SWEPT_BODY",BODY,{"disambiguationData":[OSD([sQuery(id+"F6.wireOp",EDGE,"E8.0"),sQuery(id+"F6.wireOp",EDGE,"E9.0"),sQuery(id+"F6.wireOp",EDGE,"E10"),sQuery(id+"F6.wireOp",EDGE,"E11")])]});
            var Q1;
            Q1=makeQuery(id+"F21.opExtrude","SWEPT_BODY",BODY,{"disambiguationData":[OSD([sQuery(id+"F20.wireOp",EDGE,"E38"),sQuery(id+"F20.wireOp",EDGE,"E39.0"),sQuery(id+"F20.wireOp",EDGE,"E40"),sQuery(id+"F20.wireOp",EDGE,"E41")])]});
            var Q2;
            Q2=makeQuery(id+"F19.opExtrude","SWEPT_BODY",BODY,{"disambiguationData":[OSD([sQuery(id+"F18.wireOp",EDGE,"E32"),sQuery(id+"F18.wireOp",EDGE,"E33"),sQuery(id+"F18.wireOp",EDGE,"E34.0"),sQuery(id+"F18.wireOp",EDGE,"E35.0"),sQuery(id+"F18.wireOp",EDGE,"E36"),sQuery(id+"F18.wireOp",EDGE,"E37")])]});
            var Q3;
            Q3=makeQuery(id+"F5.opExtrude","SWEPT_BODY",BODY,{"disambiguationData":[OSD([sQuery(id+"F4.wireOp",EDGE,"E4"),sQuery(id+"F4.wireOp",EDGE,"E5.0"),sQuery(id+"F4.wireOp",EDGE,"E6"),sQuery(id+"F4.wireOp",EDGE,"E7")])]});
            var Q4;
            Q4=makeQuery(id+"F17.opExtrude","SWEPT_BODY",BODY,{"disambiguationData":[OSD([sQuery(id+"F16.wireOp",EDGE,"E28"),sQuery(id+"F16.wireOp",EDGE,"E29.0"),sQuery(id+"F16.wireOp",EDGE,"E30"),sQuery(id+"F16.wireOp",EDGE,"E31")])]});
            var Q5;
            Q5=qCreatedBy(id+"F26.planeOp",FACE);
            mirror(context, id + "F27", {"entities" : qUnion([Q0, Q1, Q2, Q3, Q4]), "mirrorPlane" : qUnion([Q5])});
        }
        {
            var Q0;
            Q0=qCreatedBy(makeId("Top.planeOp"),FACE);
            var sketch = newSketch(context, id + "F28", { "sketchPlane" : qUnion([Q0])});
            skLineSegment(sketch, "E48", {"start": v(0, 0) * mm, "end": v(97.2, 234.67) * mm, "construction": true});
            skSolve(sketch);
        }
        {
            var Q0;
            Q0=sQuery(id+"F28.wireOp",EDGE,"E48");
            cPlane(context, id + "F29", {"entities" : qUnion([Q0]), "cplaneType" : CPlaneType.LINE_ANGLE, "offset" : 25.4 * mm, "angle" : 90 * degree, "width" : 152.4 * mm, "height" : 152.4 * mm});
        }
        {
            var Q0;
            Q0=makeQuery(id+"F5.opExtrude","SWEPT_BODY",BODY,{"disambiguationData":[OSD([sQuery(id+"F4.wireOp",EDGE,"E4"),sQuery(id+"F4.wireOp",EDGE,"E5.0"),sQuery(id+"F4.wireOp",EDGE,"E6"),sQuery(id+"F4.wireOp",EDGE,"E7")])]});
            var Q1;
            Q1=makeQuery(id+"F17.opExtrude","SWEPT_BODY",BODY,{"disambiguationData":[OSD([sQuery(id+"F16.wireOp",EDGE,"E28"),sQuery(id+"F16.wireOp",EDGE,"E29.0"),sQuery(id+"F16.wireOp",EDGE,"E30"),sQuery(id+"F16.wireOp",EDGE,"E31")])]});
            var Q2;
            Q2=makeQuery(id+"F7.opExtrude","SWEPT_BODY",BODY,{"disambiguationData":[OSD([sQuery(id+"F6.wireOp",EDGE,"E8.0"),sQuery(id+"F6.wireOp",EDGE,"E9.0"),sQuery(id+"F6.wireOp",EDGE,"E10"),sQuery(id+"F6.wireOp",EDGE,"E11")])]});
            var Q3;
            Q3=makeQuery(id+"F19.opExtrude","SWEPT_BODY",BODY,{"disambiguationData":[OSD([sQuery(id+"F18.wireOp",EDGE,"E32"),sQuery(id+"F18.wireOp",EDGE,"E33"),sQuery(id+"F18.wireOp",EDGE,"E34.0"),sQuery(id+"F18.wireOp",EDGE,"E35.0"),sQuery(id+"F18.wireOp",EDGE,"E36"),sQuery(id+"F18.wireOp",EDGE,"E37")])]});
            var Q4;
            Q4=makeQuery(id+"F21.opExtrude","SWEPT_BODY",BODY,{"disambiguationData":[OSD([sQuery(id+"F20.wireOp",EDGE,"E38"),sQuery(id+"F20.wireOp",EDGE,"E39.0"),sQuery(id+"F20.wireOp",EDGE,"E40"),sQuery(id+"F20.wireOp",EDGE,"E41")])]});
            var Q5;
            Q5=qCreatedBy(id+"F29.planeOp",FACE);
            mirror(context, id + "F30", {"entities" : qUnion([Q0, Q1, Q2, Q3, Q4]), "mirrorPlane" : qUnion([Q5])});
        }
    });
